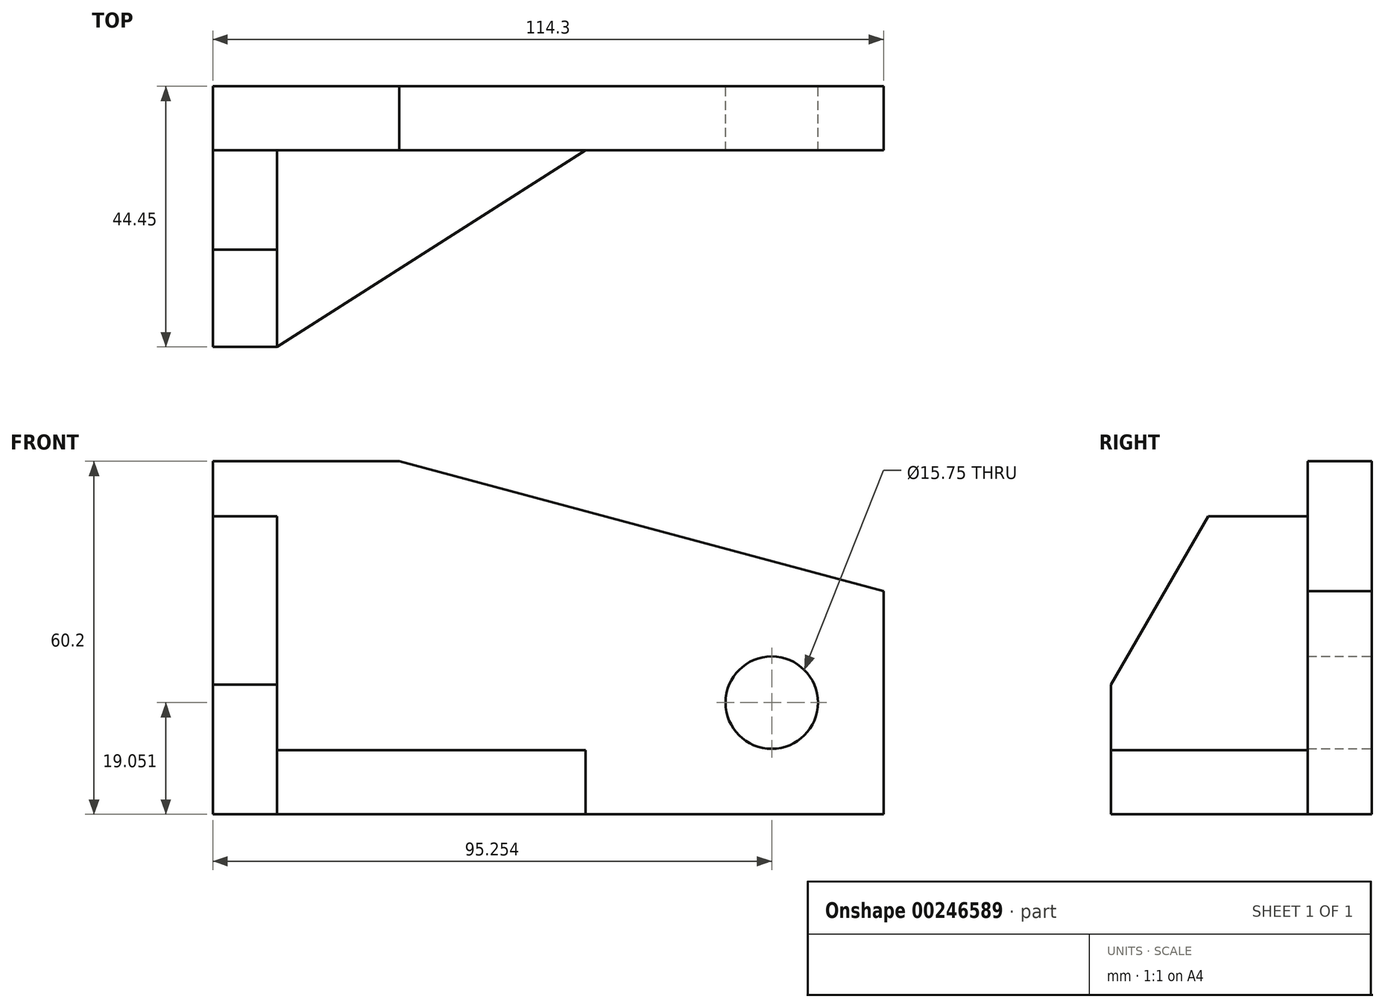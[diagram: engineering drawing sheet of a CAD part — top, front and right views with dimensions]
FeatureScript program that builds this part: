
annotation { "Feature Type Name" : "Feature", "Feature Type Description" : "" }
export const myFeature = defineFeature(function(context is Context, id is Id, definition is map)
    precondition{}
    {
        {
            var Q0;
            Q0=qCreatedBy(makeId("Front.planeOp"),FACE);
            var sketch = newSketch(context, id + "F0", { "sketchPlane" : qUnion([Q0])});
            skLineSegment(sketch, "E0", {"start": v(-59.23, 22.12) * mm, "end": v(-59.23, -38.08) * mm});
            skLineSegment(sketch, "E1", {"start": v(-59.23, -38.08) * mm, "end": v(55.07, -38.08) * mm});
            skLineSegment(sketch, "E2", {"start": v(-59.23, 22.12) * mm, "end": v(-27.48, 22.12) * mm});
            skLineSegment(sketch, "E3", {"start": v(-27.48, 22.12) * mm, "end": v(55.07, 0) * mm});
            skLineSegment(sketch, "E4", {"start": v(55.07, 0) * mm, "end": v(55.07, -38.08) * mm});
            skCircle(sketch, "E5", {"center": v(36.02, -19.03) * mm, "radius": 7.87 * mm});
            skSolve(sketch);
        }
        {
            var Q0;
            Q0=makeQuery(id+"F0.imprint","IMPRINT",FACE,{"disambiguationData":[TD([[makeQuery(id+"F0.imprint","IMPRINT",EDGE,{"derivedFrom":sQuery(id+"F0.wireOp",EDGE,"E0")}),1.0]])]});
            extrude(context, id + "F1", {"entities" : qUnion([Q0]), "depth" : 10.92 * mm});
        }
        {
            var Q0;
            Q0=makeQuery(id+"F1.opExtrude","SWEPT_FACE",FACE,{"disambiguationData":[OSD([sQuery(id+"F0.wireOp",EDGE,"E1")])]});
            var sketch = newSketch(context, id + "F2", { "sketchPlane" : qUnion([Q0])});
            skLineSegment(sketch, "E6", {"start": v(-59.23, 10.92) * mm, "end": v(-59.23, 44.45) * mm});
            skLineSegment(sketch, "E7", {"start": v(-59.23, 44.45) * mm, "end": v(-48.3, 44.45) * mm});
            skLineSegment(sketch, "E8", {"start": v(-48.3, 44.45) * mm, "end": v(4.27, 10.92) * mm});
            skSolve(sketch);
        }
        {
            var Q0;
            {var subQ0=sQuery(id+"F2.wireOp",EDGE,"E6");Q0=makeQuery(id+"F2.imprint","IMPRINT",FACE,{"disambiguationData":[TD([[makeQuery(id+"F2.imprint","IMPRINT",EDGE,{"derivedFrom":subQ0}),-1.0]])]});}
            extrude(context, id + "F3", {"entities" : qUnion([Q0]), "operationType" : NewBodyOperationType.ADD, "oppositeDirection" : true, "depth" : 10.92 * mm});
        }
        {
            var Q0;
            Q0=makeQuery(id+"F3.boolean.opBoolean","MERGE",FACE,{"derivedFrom":[makeQuery(id+"F1.opExtrude","SWEPT_FACE",FACE,{"disambiguationData":[OSD([sQuery(id+"F0.wireOp",EDGE,"E0")])]}),makeQuery(id+"F3.opExtrude","SWEPT_FACE",FACE,{"disambiguationData":[OSD([sQuery(id+"F2.wireOp",EDGE,"E6")])]})]});
            var sketch = newSketch(context, id + "F4", { "sketchPlane" : qUnion([Q0])});
            skLineSegment(sketch, "E9", {"start": v(10.92, 12.72) * mm, "end": v(27.88, 12.72) * mm});
            skLineSegment(sketch, "E10", {"start": v(44.45, -27.16) * mm, "end": v(44.45, -15.98) * mm});
            skLineSegment(sketch, "E11", {"start": v(44.45, -15.98) * mm, "end": v(27.88, 12.72) * mm});
            skLineSegment(sketch, "E12", {"start": v(44.45, -27.16) * mm, "end": v(44.45, 42.65) * mm, "construction": true});
            skSolve(sketch);
        }
        {
            var Q0;
            {var subQ1=sQuery(id+"F4.wireOp",EDGE,"E9");Q0=makeQuery(id+"F4.imprint","IMPRINT",FACE,{"disambiguationData":[TD([[makeQuery(id+"F4.imprint","IMPRINT",EDGE,{"derivedFrom":subQ1}),-1.0]])]});}
            extrude(context, id + "F5", {"entities" : qUnion([Q0]), "operationType" : NewBodyOperationType.ADD, "oppositeDirection" : true, "depth" : 10.92 * mm});
        }
    });
